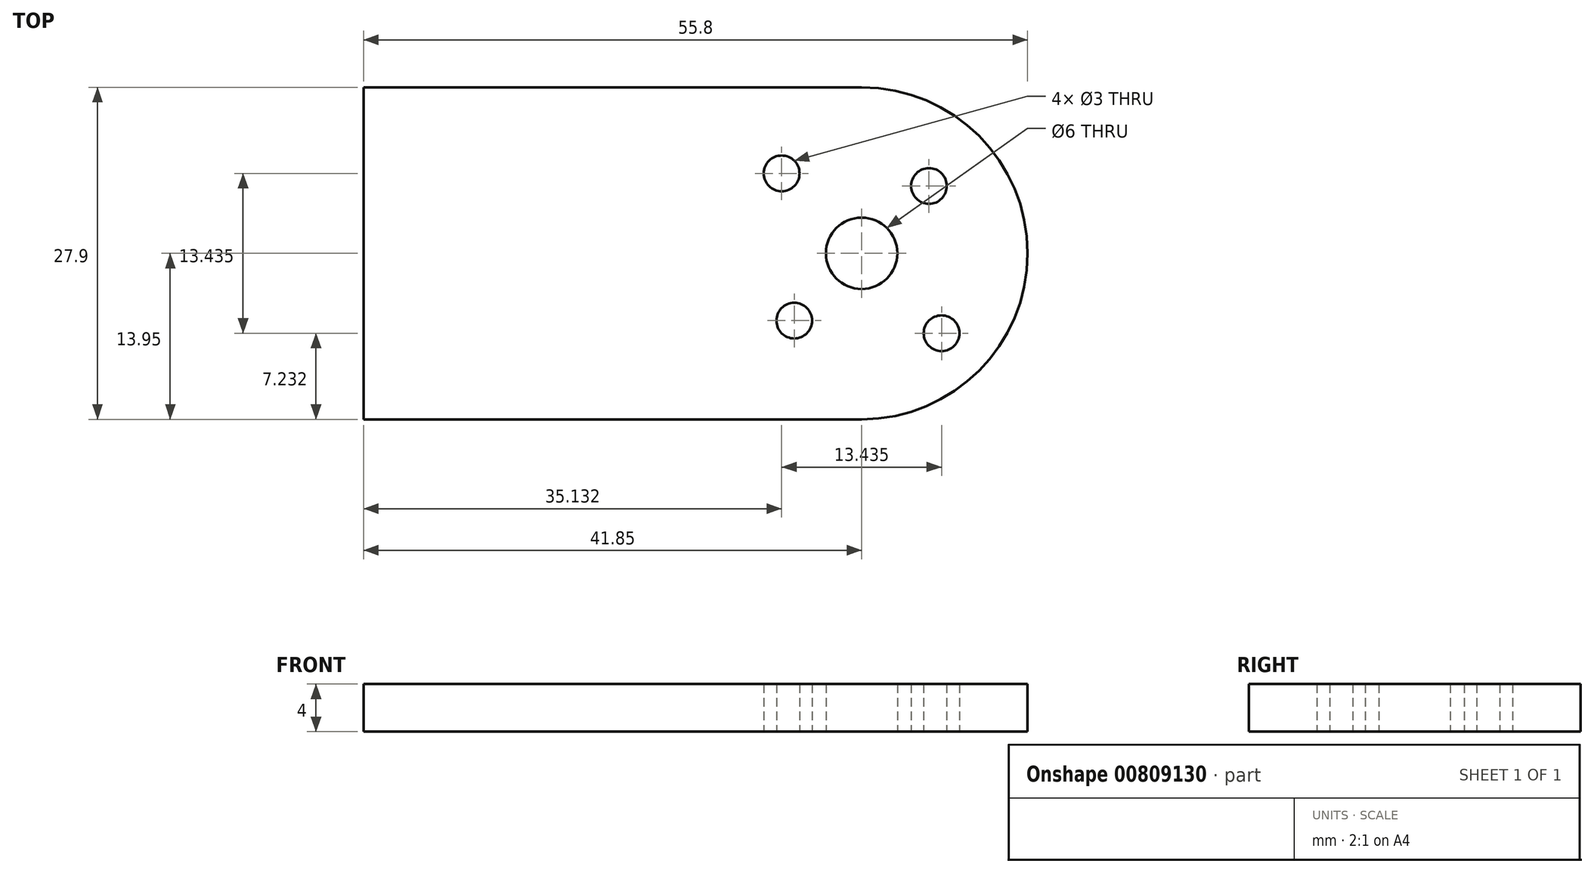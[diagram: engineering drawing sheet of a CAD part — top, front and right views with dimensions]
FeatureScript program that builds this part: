
annotation { "Feature Type Name" : "Feature", "Feature Type Description" : "" }
export const myFeature = defineFeature(function(context is Context, id is Id, definition is map)
    precondition{}
    {
        {
            var Q0;
            Q0=qCreatedBy(makeId("Top.planeOp"),FACE);
            var sketch = newSketch(context, id + "F0", { "sketchPlane" : qUnion([Q0])});
            skLineSegment(sketch, "E0.bottom", {"start": v(0, 0) * mm, "end": v(-55.8, 0) * mm});
            skLineSegment(sketch, "E0.top", {"start": v(0, 27.9) * mm, "end": v(-55.8, 27.9) * mm});
            skLineSegment(sketch, "E0.left", {"start": v(0, 0) * mm, "end": v(0, 27.9) * mm});
            skLineSegment(sketch, "E0.right", {"start": v(-55.8, 0) * mm, "end": v(-55.8, 27.9) * mm});
            skLineSegment(sketch, "E1", {"start": v(-13.95, 27.9) * mm, "end": v(-13.95, 0) * mm, "construction": true});
            skCircle(sketch, "E2", {"center": v(-13.95, 13.95) * mm, "radius": 8 * mm, "construction": true});
            skCircle(sketch, "E3", {"center": v(-13.95, 13.95) * mm, "radius": 9.5 * mm, "construction": true});
            skLineSegment(sketch, "E4", {"start": v(-21.95, 13.95) * mm, "end": v(-5.95, 13.95) * mm, "construction": true});
            skLineSegment(sketch, "E5", {"start": v(-19.6, 8.3) * mm, "end": v(-8.3, 19.6) * mm, "construction": true});
            skLineSegment(sketch, "E6", {"start": v(-20.67, 20.67) * mm, "end": v(-7.23, 7.23) * mm, "construction": true});
            skCircle(sketch, "E7", {"center": v(-8.3, 19.6) * mm, "radius": 1.5 * mm});
            skCircle(sketch, "E8", {"center": v(-19.6, 8.3) * mm, "radius": 1.5 * mm});
            skCircle(sketch, "E9", {"center": v(-20.67, 20.67) * mm, "radius": 1.5 * mm});
            skCircle(sketch, "E10", {"center": v(-7.23, 7.23) * mm, "radius": 1.5 * mm});
            skCircle(sketch, "E11", {"center": v(-13.95, 13.95) * mm, "radius": 3 * mm});
            skSolve(sketch);
        }
        {
            var Q0;
            Q0=makeQuery(id+"F0.imprint","IMPRINT",FACE,{"disambiguationData":[TD([[makeQuery(id+"F0.imprint","IMPRINT",EDGE,{"derivedFrom":sQuery(id+"F0.wireOp",EDGE,"E0.bottom")}),-1.0]])]});
            extrude(context, id + "F1", {"entities" : qUnion([Q0]), "depth" : 4 * mm, "offsetDistance" : 25.4 * mm});
        }
        {
            var Q0;
            Q0=makeQuery(id+"F1.opExtrude","SWEPT_EDGE",EDGE,{"disambiguationData":[OSD([sQuery(id+"F0.wireOp",EDGE,"E0.top"),sQuery(id+"F0.wireOp",EDGE,"E0.left")])]});
            var Q1;
            Q1=makeQuery(id+"F1.opExtrude","SWEPT_EDGE",EDGE,{"disambiguationData":[OSD([sQuery(id+"F0.wireOp",EDGE,"E0.bottom"),sQuery(id+"F0.wireOp",EDGE,"E0.left")])]});
            fillet(context, id + "F2", {"entities" : qUnion([Q0, Q1]), "radius" : (27.9 / 2) * mm, "tangentPropagation" : true, "allowEdgeOverflow" : false});
        }
    });
